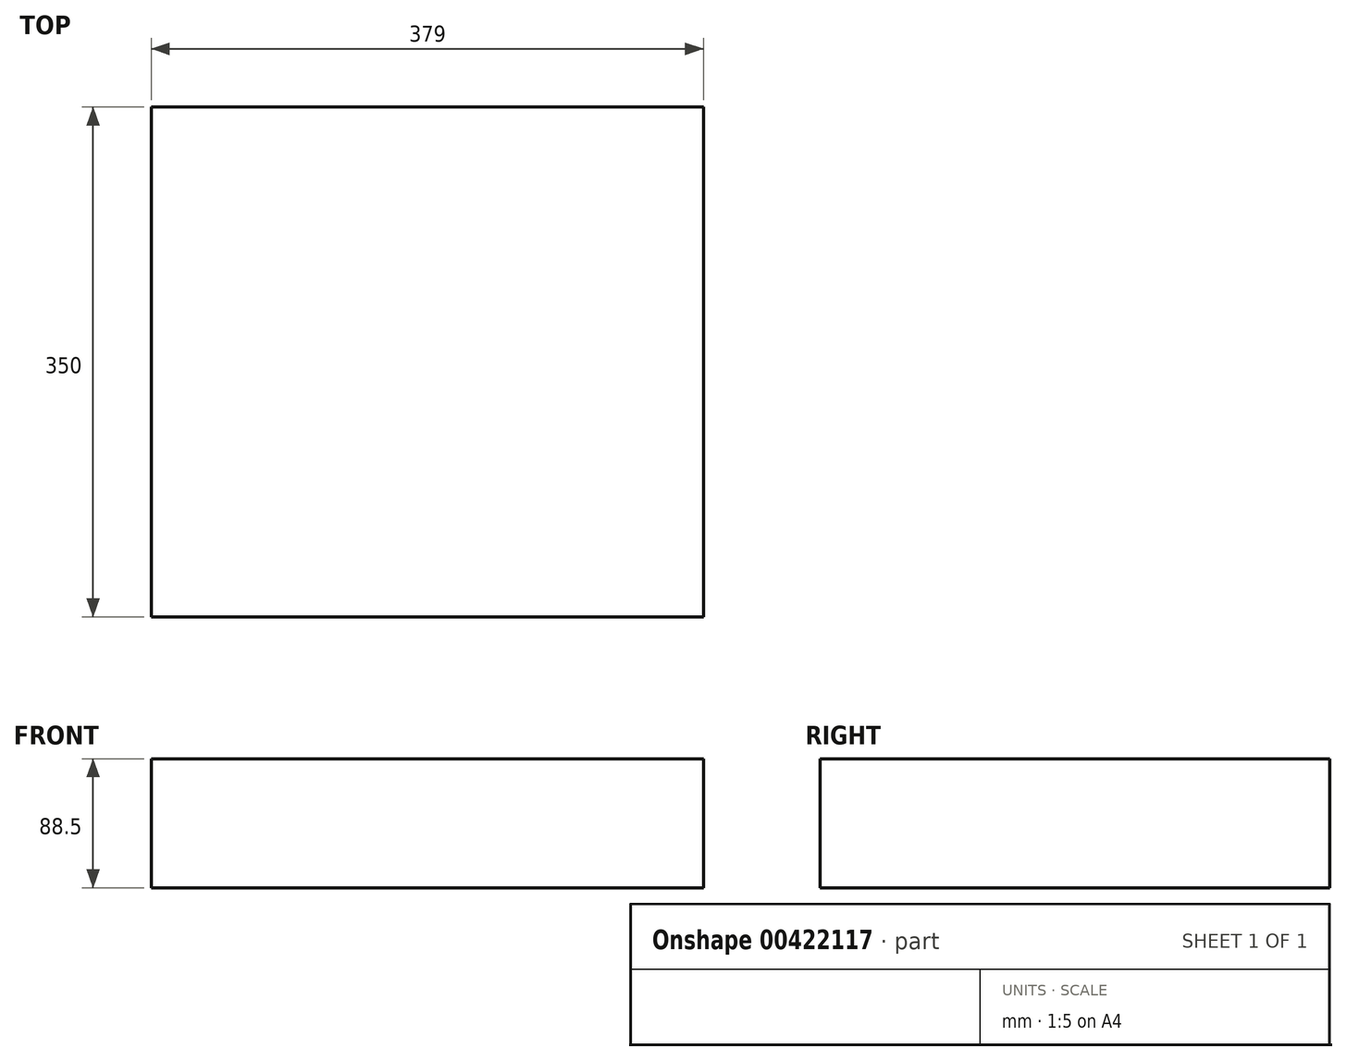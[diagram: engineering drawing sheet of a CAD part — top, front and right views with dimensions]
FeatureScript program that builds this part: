
annotation { "Feature Type Name" : "Feature", "Feature Type Description" : "" }
export const myFeature = defineFeature(function(context is Context, id is Id, definition is map)
    precondition{}
    {
        {
            var Q0;
            Q0=qCreatedBy(makeId("Front.planeOp"),FACE);
            var sketch = newSketch(context, id + "F0", { "sketchPlane" : qUnion([Q0])});
            skLineSegment(sketch, "E0.bottom", {"start": v(189.5, 44.25) * mm, "end": v(-189.5, 44.25) * mm});
            skLineSegment(sketch, "E0.top", {"start": v(189.5, -44.25) * mm, "end": v(-189.5, -44.25) * mm});
            skLineSegment(sketch, "E0.left", {"start": v(189.5, 44.25) * mm, "end": v(189.5, -44.25) * mm});
            skLineSegment(sketch, "E0.right", {"start": v(-189.5, 44.25) * mm, "end": v(-189.5, -44.25) * mm});
            skPoint(sketch, "E0.middle", {"position": v(0, 0) * mm});
            skSolve(sketch);
        }
        {
            var Q0;
            Q0 = qSketchRegion(id + "F0", true);
            extrude(context, id + "F1", {"entities" : qUnion([Q0]), "depth" : 350 * mm});
        }
    });
